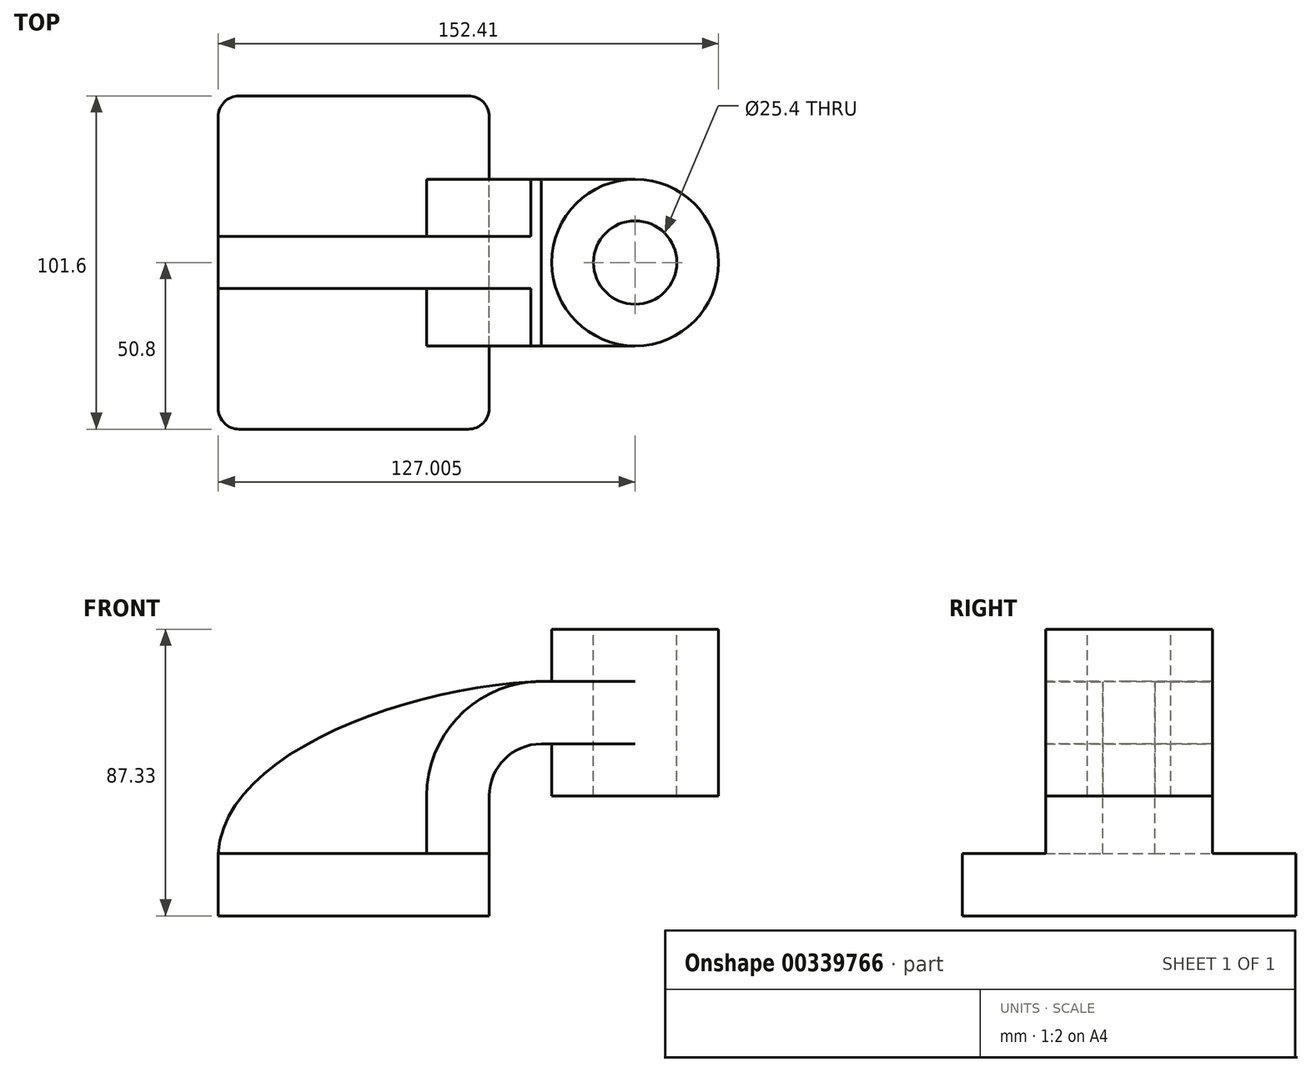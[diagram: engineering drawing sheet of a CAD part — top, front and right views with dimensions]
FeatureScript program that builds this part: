
annotation { "Feature Type Name" : "Feature", "Feature Type Description" : "" }
export const myFeature = defineFeature(function(context is Context, id is Id, definition is map)
    precondition{}
    {
        {
            var Q0;
            Q0=qCreatedBy(makeId("Front.planeOp"),FACE);
            var sketch = newSketch(context, id + "F0", { "sketchPlane" : qUnion([Q0])});
            skLineSegment(sketch, "E0.rect.bottom", {"start": v(-41.28, 9.52) * mm, "end": v(41.28, 9.52) * mm});
            skLineSegment(sketch, "E0.rect.top", {"start": v(-41.28, -9.52) * mm, "end": v(41.28, -9.52) * mm});
            skLineSegment(sketch, "E0.rect.left", {"start": v(-41.28, 9.52) * mm, "end": v(-41.28, -9.52) * mm});
            skLineSegment(sketch, "E0.rect.right", {"start": v(41.28, 9.52) * mm, "end": v(41.28, -9.52) * mm});
            skPoint(sketch, "E0.rect.middle", {"position": v(0, 0) * mm});
            skLineSegment(sketch, "E1", {"start": v(41.28, 9.52) * mm, "end": v(41.28, 27) * mm});
            skArc(sketch, "E2", {"start": v(41.28, 27) * mm, "mid": v(45.92, 38.23) * mm, "end": v(57.15, 42.88) * mm});
            skLineSegment(sketch, "E3", {"start": v(57.15, 42.88) * mm, "end": v(85.72, 42.88) * mm});
            skLineSegment(sketch, "E4.rect.bottom", {"start": v(60.32, 27) * mm, "end": v(111.12, 27) * mm});
            skLineSegment(sketch, "E4.rect.top", {"start": v(60.32, 77.8) * mm, "end": v(111.12, 77.8) * mm});
            skLineSegment(sketch, "E4.rect.left", {"start": v(60.32, 27) * mm, "end": v(60.32, 77.8) * mm});
            skLineSegment(sketch, "E4.rect.right", {"start": v(111.13, 27) * mm, "end": v(111.12, 77.8) * mm});
            skPoint(sketch, "E4.rect.middle", {"position": v(85.72, 52.4) * mm});
            skLineSegment(sketch, "E5.0", {"start": v(57.15, 61.93) * mm, "end": v(85.72, 61.93) * mm});
            skArc(sketch, "E5.1", {"start": v(22.23, 27) * mm, "mid": v(32.45, 51.7) * mm, "end": v(57.15, 61.93) * mm});
            skLineSegment(sketch, "E5.2", {"start": v(22.23, 9.52) * mm, "end": v(22.23, 27) * mm});
            skLineSegment(sketch, "E6", {"start": v(85.72, 27) * mm, "end": v(85.72, 77.8) * mm});
            skFitSpline(sketch, "E7", {"points": [v(-41.28, 9.53) * mm, v(57.15, 61.93) * mm], "startDerivative": vector(5.2, 92.34) * mm, "endDerivative": vector(120.92, 4.22) * mm});
            skLineSegment(sketch, "E8", {"start": v(57.15, 42.88) * mm, "end": v(57.15, 61.93) * mm, "construction": true});
            skLineSegment(sketch, "E9", {"start": v(57.15, 52.4) * mm, "end": v(74, 52.4) * mm, "construction": true});
            skSolve(sketch);
        }
        {
            var Q0;
            Q0=makeQuery(id+"F0.imprint","IMPRINT",FACE,{"disambiguationData":[TD([[makeQuery(id+"F0.imprint","IMPRINT",EDGE,{"derivedFrom":sQuery(id+"F0.wireOp",EDGE,"E0.rect.top")}),1.0]])]});
            extrude(context, id + "F1", {"entities" : qUnion([Q0]), "depth" : 101.6 * mm, "symmetric" : true});
        }
        {
            var Q0;
            {var subQ9=sQuery(id+"F0.wireOp",EDGE,"E1");Q0=makeQuery(id+"F0.imprint","IMPRINT",FACE,{"disambiguationData":[TD([[makeQuery(id+"F0.imprint","IMPRINT",EDGE,{"derivedFrom":subQ9}),1.0]])]});}
            var Q1;
            {var subQ0=sQuery(id+"F0.wireOp",EDGE,"E6");var subQ1=sQuery(id+"F0.wireOp",EDGE,"E3");var subQ2=makeQuery(id+"F0.imprint","INTERSECT",VERTEX,{"derivedFrom":[subQ1,subQ0]});Q1=makeQuery(id+"F0.imprint","IMPRINT",FACE,{"disambiguationData":[TD([[makeQuery(id+"F0.imprint","IMPRINT",EDGE,{"disambiguationData":[TD([[subQ2,1.0]])],"derivedFrom":subQ1}),1.0]])]});}
            extrude(context, id + "F2", {"entities" : qUnion([Q0, Q1]), "operationType" : NewBodyOperationType.ADD, "depth" : 50.8 * mm, "symmetric" : true});
        }
        {
            var Q0;
            {var subQ3=sQuery(id+"F0.wireOp",EDGE,"E5.2");Q0=makeQuery(id+"F0.imprint","IMPRINT",FACE,{"disambiguationData":[TD([[makeQuery(id+"F0.imprint","IMPRINT",EDGE,{"derivedFrom":subQ3}),1.0]])]});}
            extrude(context, id + "F3", {"entities" : qUnion([Q0]), "operationType" : NewBodyOperationType.ADD, "depth" : 15.88 * mm, "symmetric" : true});
        }
        {
            var Q0;
            {var subQ5=sQuery(id+"F0.wireOp",EDGE,"E4.rect.right");Q0=makeQuery(id+"F0.imprint","IMPRINT",FACE,{"disambiguationData":[TD([[makeQuery(id+"F0.imprint","IMPRINT",EDGE,{"derivedFrom":subQ5}),1.0]])]});}
            var Q1;
            Q1=sQuery(id+"F0.wireOp",EDGE,"E6");
            revolve(context, id + "F4", {"operationType" : NewBodyOperationType.ADD, "entities" : qUnion([Q0]), "axis" : qUnion([Q1]), "revolveType" : RevolveType.FULL});
        }
        {
            var Q0;
            Q0=makeQuery(id+"F1.opExtrude","CAP_EDGE",EDGE,{"disambiguationData":[OSD([sQuery(id+"F0.wireOp",EDGE,"E0.rect.right")])],"isStart":false});
            var Q1;
            Q1=makeQuery(id+"F1.opExtrude","CAP_EDGE",EDGE,{"disambiguationData":[OSD([sQuery(id+"F0.wireOp",EDGE,"E0.rect.left")])],"isStart":false});
            var Q2;
            Q2=makeQuery(id+"F1.opExtrude","CAP_EDGE",EDGE,{"disambiguationData":[OSD([sQuery(id+"F0.wireOp",EDGE,"E0.rect.right")])],"isStart":true});
            var Q3;
            Q3=makeQuery(id+"F1.opExtrude","CAP_EDGE",EDGE,{"disambiguationData":[OSD([sQuery(id+"F0.wireOp",EDGE,"E0.rect.left")])],"isStart":true});
            fillet(context, id + "F5", {"entities" : qUnion([Q0, Q1, Q2, Q3]), "radius" : 6.35 * mm, "tangentPropagation" : true, "allowEdgeOverflow" : false});
        }
        {
            var Q0;
            Q0=makeQuery(id+"F4.opRevolve","SWEPT_FACE",FACE,{"disambiguationData":[OSD([sQuery(id+"F0.wireOp",EDGE,"E4.rect.top")])]});
            var sketch = newSketch(context, id + "F6", { "sketchPlane" : qUnion([Q0])});
            skCircle(sketch, "E10.0", {"center": v(85.72, 0) * mm, "radius": 12.7 * mm});
            skSolve(sketch);
        }
        {
            var Q0;
            Q0=makeQuery(id+"F6.imprint","IMPRINT",FACE,{"disambiguationData":[TD([[makeQuery(id+"F6.imprint","IMPRINT",EDGE,{"derivedFrom":sQuery(id+"F6.wireOp",EDGE,"E10.0")}),1.0]])]});
            extrude(context, id + "F7", {"entities" : qUnion([Q0]), "operationType" : NewBodyOperationType.REMOVE, "endBound" : BoundingType.UP_TO_NEXT, "oppositeDirection" : true, "depth" : 25.4 * mm});
        }
    });
